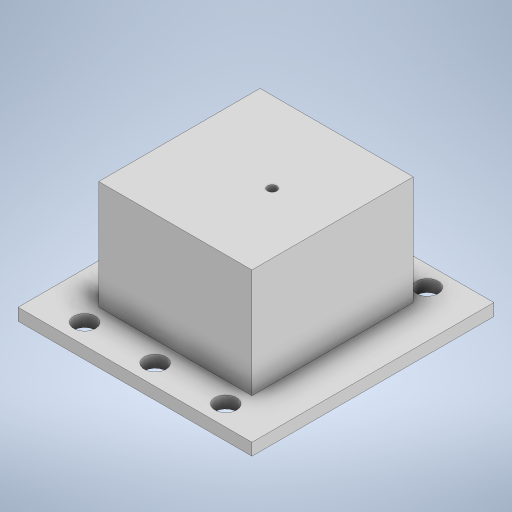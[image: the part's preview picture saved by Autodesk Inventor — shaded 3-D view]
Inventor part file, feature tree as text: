
AUTODESK INVENTOR PART (.ipt)
format: ipt  version: 2024 (Build 280153000, 153)  size: 310,784 bytes
history: native  units: mm
features: extrude x6, sketch x6, plane x3
ambient origin geometry x8: Origin, YZ Plane, XZ Plane, XY Plane, X Axis, Y Axis, Z Axis, Center Point
bodies: Body1 (feature_tree)
feature tree (15):
  plane  "Work Plane5"
  extrude  "Extrusion34"  Depth=40.0mm
  plane  "Work Plane2"
  extrude  "Extrusion35"  Depth=30.0mm
  plane  "Work Plane1"
  extrude  "Extrusion51"  Depth=30.0mm
  sketch  "Sketch77"  dims[d211=10.0mm d212=0.0mm d219=35.0mm]
  extrude  "Extrusion53"  Depth=10.0mm
  extrude  "Extrusion54"  Depth=60.0mm
  extrude  "Extrusion56"  Depth=3.0mm TaperAngle=0.0deg
  sketch  "Sketch45"  dims[d142=38.0mm d143=40.0mm]
  sketch  "Sketch47"  dims[d144=30.0mm d145=0.0mm d146=36.0mm]
  sketch  "Sketch74"  dims[d147=30.0mm d148=-2.617994mm d210=2.3mm]
  sketch  "Sketch78"  dims[d220=58.0mm d221=60.0mm]
  sketch  "Sketch81"  dims[d222=3.0mm d223=0.0mm d224=3.0mm d225=0.0mm d232=5.0mm d233=11.5mm d234=5.4mm d235=17.5mm d236=5.4mm d237=17.5mm d238=5.4mm d239=5.0mm d240=17.0mm d241=5.4mm d242=16.0mm d243=5.4mm d244=17.0mm d245=5.4mm d246=17.5mm d247=5.4mm d248=17.5mm d249=5.0mm d250=30.0mm d251=0.0mm d49=0.5mm d50=0.872665mm d51=0.5mm d52=0.872665mm d130=0.5mm d131=0.872665mm d132=0.5mm d133=0.872665mm d156=0.5mm d157=0.872665mm d158=0.5mm d159=0.872665mm d173=0.5mm d174=0.872665mm d175=0.5mm d176=0.872665mm d226=0.5mm d227=0.872665mm]
